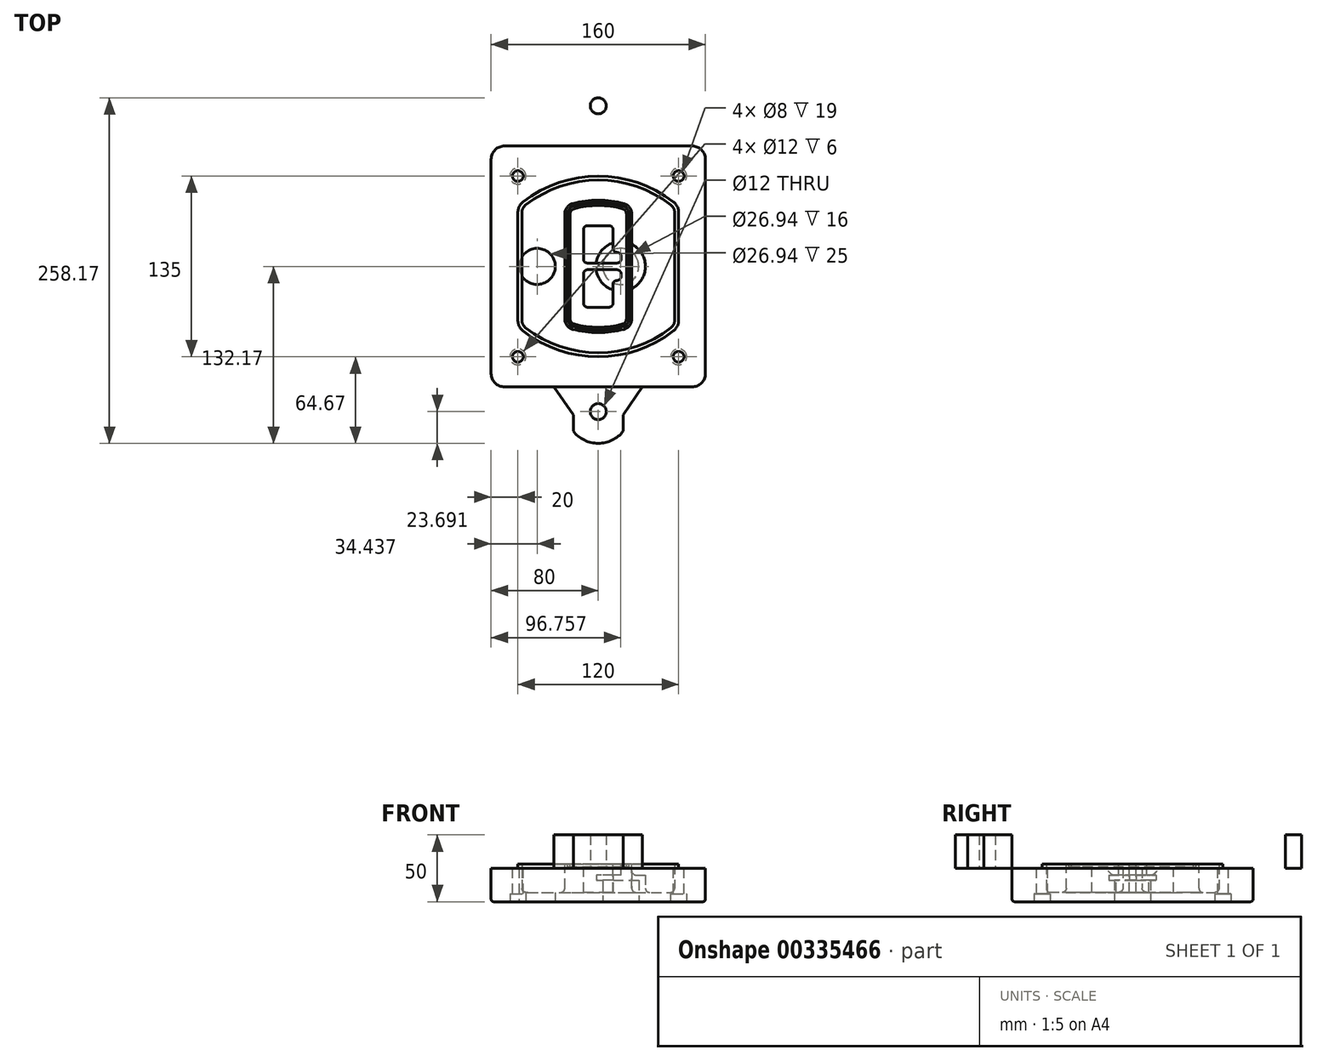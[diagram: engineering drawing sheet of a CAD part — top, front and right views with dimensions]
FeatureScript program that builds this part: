
annotation { "Feature Type Name" : "Feature", "Feature Type Description" : "" }
export const myFeature = defineFeature(function(context is Context, id is Id, definition is map)
    precondition{}
    {
        {
            var Q0;
            Q0=qCreatedBy(makeId("Top.planeOp"),FACE);
            var sketch = newSketch(context, id + "F0", { "sketchPlane" : qUnion([Q0])});
            skPoint(sketch, "E0.rect.middle", {"position": v(0, 0) * mm});
            skLineSegment(sketch, "E1.bottom", {"start": v(-70, -90) * mm, "end": v(70, -90) * mm});
            skLineSegment(sketch, "E1.top", {"start": v(-70, 90) * mm, "end": v(70, 90) * mm});
            skLineSegment(sketch, "E1.left", {"start": v(-80, -80) * mm, "end": v(-80, 80) * mm});
            skLineSegment(sketch, "E1.right", {"start": v(80, -80) * mm, "end": v(80, 80) * mm});
            skLineSegment(sketch, "E2", {"start": v(-80, 90) * mm, "end": v(80, -90) * mm, "construction": true});
            skLineSegment(sketch, "E3", {"start": v(80, 90) * mm, "end": v(-80, -90) * mm, "construction": true});
            skCircle(sketch, "E4", {"center": v(-60, 67.5) * mm, "radius": 4 * mm});
            skCircle(sketch, "E5", {"center": v(60, 67.5) * mm, "radius": 4 * mm});
            skCircle(sketch, "E6", {"center": v(60, -67.5) * mm, "radius": 4 * mm});
            skCircle(sketch, "E7", {"center": v(-60, -67.5) * mm, "radius": 4 * mm});
            skLineSegment(sketch, "E8", {"start": v(-60, 67.5) * mm, "end": v(60, 67.5) * mm, "construction": true});
            skLineSegment(sketch, "E9", {"start": v(60, 67.5) * mm, "end": v(60, -67.5) * mm, "construction": true});
            skLineSegment(sketch, "E10", {"start": v(60, -67.5) * mm, "end": v(-60, -67.5) * mm, "construction": true});
            skLineSegment(sketch, "E11", {"start": v(-60, -67.5) * mm, "end": v(-60, 67.5) * mm, "construction": true});
            skLineSegment(sketch, "E12", {"start": v(-60, 40.3) * mm, "end": v(-60, -40.3) * mm});
            skLineSegment(sketch, "E13", {"start": v(60, 40.3) * mm, "end": v(60, -40.3) * mm});
            skArc(sketch, "E14", {"start": v(56.15, 48.18) * mm, "mid": v(0, 67.5) * mm, "end": v(-56.15, 48.18) * mm});
            skArc(sketch, "E15", {"start": v(-56.15, -48.18) * mm, "mid": v(0, -67.5) * mm, "end": v(56.15, -48.18) * mm});
            skLineSegment(sketch, "E16", {"start": v(-60, 0) * mm, "end": v(60, 0) * mm, "construction": true});
            skPoint(sketch, "E17.visualSharp", {"position": v(-60, -45) * mm});
            skArc(sketch, "E17.filletArc", {"start": v(-60, -40.3) * mm, "mid": v(-58.99, -44.68) * mm, "end": v(-56.15, -48.18) * mm});
            skPoint(sketch, "E18.visualSharp", {"position": v(-60, 45) * mm});
            skArc(sketch, "E18.filletArc", {"start": v(-56.15, 48.18) * mm, "mid": v(-58.99, 44.68) * mm, "end": v(-60, 40.3) * mm});
            skPoint(sketch, "E19.visualSharp", {"position": v(60, 45) * mm});
            skArc(sketch, "E19.filletArc", {"start": v(60, 40.3) * mm, "mid": v(58.99, 44.68) * mm, "end": v(56.15, 48.18) * mm});
            skPoint(sketch, "E20.visualSharp", {"position": v(60, -45) * mm});
            skArc(sketch, "E20.filletArc", {"start": v(56.15, -48.18) * mm, "mid": v(58.99, -44.68) * mm, "end": v(60, -40.3) * mm});
            skPoint(sketch, "E21.visualSharp", {"position": v(-80, 90) * mm});
            skArc(sketch, "E21.filletArc", {"start": v(-70, 90) * mm, "mid": v(-77.07, 87.07) * mm, "end": v(-80, 80) * mm});
            skPoint(sketch, "E22.visualSharp", {"position": v(80, 90) * mm});
            skArc(sketch, "E22.filletArc", {"start": v(80, 80) * mm, "mid": v(77.07, 87.07) * mm, "end": v(70, 90) * mm});
            skPoint(sketch, "E23.visualSharp", {"position": v(80, -90) * mm});
            skArc(sketch, "E23.filletArc", {"start": v(70, -90) * mm, "mid": v(77.07, -87.07) * mm, "end": v(80, -80) * mm});
            skPoint(sketch, "E24.visualSharp", {"position": v(-80, -90) * mm});
            skArc(sketch, "E24.filletArc", {"start": v(-80, -80) * mm, "mid": v(-77.07, -87.07) * mm, "end": v(-70, -90) * mm});
            skArc(sketch, "E25.0", {"start": v(57, 40.3) * mm, "mid": v(56.3, 43.36) * mm, "end": v(54.3, 45.81) * mm});
            skLineSegment(sketch, "E25.1", {"start": v(57, 40.3) * mm, "end": v(57, -40.3) * mm});
            skArc(sketch, "E25.2", {"start": v(54.3, -45.81) * mm, "mid": v(56.3, -43.36) * mm, "end": v(57, -40.3) * mm});
            skArc(sketch, "E25.3", {"start": v(-54.3, -45.81) * mm, "mid": v(0, -64.5) * mm, "end": v(54.3, -45.81) * mm});
            skArc(sketch, "E25.4", {"start": v(-57, -40.3) * mm, "mid": v(-56.3, -43.36) * mm, "end": v(-54.3, -45.81) * mm});
            skArc(sketch, "E25.5", {"start": v(54.3, 45.81) * mm, "mid": v(0, 64.5) * mm, "end": v(-54.3, 45.81) * mm});
            skLineSegment(sketch, "E25.6", {"start": v(-57, 40.3) * mm, "end": v(-57, -40.3) * mm});
            skArc(sketch, "E25.7", {"start": v(-54.3, 45.81) * mm, "mid": v(-56.3, 43.36) * mm, "end": v(-57, 40.3) * mm});
            skArc(sketch, "E26.0", {"start": v(-58.62, 51.33) * mm, "mid": v(-62.58, 46.43) * mm, "end": v(-64, 40.3) * mm});
            skArc(sketch, "E26.1", {"start": v(58.62, 51.33) * mm, "mid": v(0, 71.5) * mm, "end": v(-58.62, 51.33) * mm});
            skArc(sketch, "E26.2", {"start": v(64, 40.3) * mm, "mid": v(62.58, 46.43) * mm, "end": v(58.62, 51.33) * mm});
            skLineSegment(sketch, "E26.3", {"start": v(64, 40.3) * mm, "end": v(64, -40.3) * mm});
            skArc(sketch, "E26.4", {"start": v(58.62, -51.33) * mm, "mid": v(62.58, -46.43) * mm, "end": v(64, -40.3) * mm});
            skLineSegment(sketch, "E26.5", {"start": v(-64, 40.3) * mm, "end": v(-64, -40.3) * mm});
            skArc(sketch, "E26.6", {"start": v(-58.62, -51.33) * mm, "mid": v(0, -71.5) * mm, "end": v(58.62, -51.33) * mm});
            skArc(sketch, "E26.7", {"start": v(-64, -40.3) * mm, "mid": v(-62.58, -46.43) * mm, "end": v(-58.62, -51.33) * mm});
            skSolve(sketch);
        }
        {
            var Q0;
            Q0=makeQuery(id+"F0.imprint","IMPRINT",FACE,{"disambiguationData":[TD([[makeQuery(id+"F0.imprint","IMPRINT",EDGE,{"derivedFrom":sQuery(id+"F0.wireOp",EDGE,"E1.bottom")}),1.0]])]});
            var Q1;
            Q1=makeQuery(id+"F0.imprint","IMPRINT",FACE,{"disambiguationData":[TD([[makeQuery(id+"F0.imprint","IMPRINT",EDGE,{"derivedFrom":sQuery(id+"F0.wireOp",EDGE,"E12")}),1.0]])]});
            var Q2;
            Q2=makeQuery(id+"F0.imprint","IMPRINT",FACE,{"disambiguationData":[TD([[makeQuery(id+"F0.imprint","IMPRINT",EDGE,{"derivedFrom":sQuery(id+"F0.wireOp",EDGE,"E25.0")}),1.0]])]});
            var Q3;
            Q3=makeQuery(id+"F0.imprint","IMPRINT",FACE,{"disambiguationData":[TD([[makeQuery(id+"F0.imprint","IMPRINT",EDGE,{"derivedFrom":sQuery(id+"F0.wireOp",EDGE,"E12")}),-1.0]])]});
            extrude(context, id + "F1", {"entities" : qUnion([Q0, Q1, Q2, Q3]), "oppositeDirection" : true, "depth" : 25 * mm});
        }
        {
            var Q0;
            Q0=makeQuery(id+"F0.imprint","IMPRINT",FACE,{"disambiguationData":[TD([[makeQuery(id+"F0.imprint","IMPRINT",EDGE,{"derivedFrom":sQuery(id+"F0.wireOp",EDGE,"E12")}),1.0]])]});
            extrude(context, id + "F2", {"entities" : qUnion([Q0]), "operationType" : NewBodyOperationType.ADD, "depth" : 3 * mm});
        }
        {
            var Q0;
            Q0=makeQuery(id+"F0.imprint","IMPRINT",FACE,{"disambiguationData":[TD([[makeQuery(id+"F0.imprint","IMPRINT",EDGE,{"derivedFrom":sQuery(id+"F0.wireOp",EDGE,"E25.0")}),1.0]])]});
            extrude(context, id + "F3", {"entities" : qUnion([Q0]), "operationType" : NewBodyOperationType.REMOVE, "oppositeDirection" : true, "depth" : 18 * mm});
        }
        {
            var Q0;
            Q0=makeQuery(id+"F2.opExtrude","CAP_FACE",FACE,{"disambiguationData":[OSD([sQuery(id+"F0.wireOp",EDGE,"E12"),sQuery(id+"F0.wireOp",EDGE,"E13"),sQuery(id+"F0.wireOp",EDGE,"E14"),sQuery(id+"F0.wireOp",EDGE,"E15"),sQuery(id+"F0.wireOp",EDGE,"E17.filletArc"),sQuery(id+"F0.wireOp",EDGE,"E18.filletArc"),sQuery(id+"F0.wireOp",EDGE,"E19.filletArc"),sQuery(id+"F0.wireOp",EDGE,"E20.filletArc"),sQuery(id+"F0.wireOp",EDGE,"E25.0"),sQuery(id+"F0.wireOp",EDGE,"E25.1"),sQuery(id+"F0.wireOp",EDGE,"E25.2"),sQuery(id+"F0.wireOp",EDGE,"E25.3"),sQuery(id+"F0.wireOp",EDGE,"E25.4"),sQuery(id+"F0.wireOp",EDGE,"E25.5"),sQuery(id+"F0.wireOp",EDGE,"E25.6"),sQuery(id+"F0.wireOp",EDGE,"E25.7")])],"isStart":false});
            var sketch = newSketch(context, id + "F4", { "sketchPlane" : qUnion([Q0])});
            skArc(sketch, "E27.0", {"start": v(-19.08, -46.97) * mm, "mid": v(0, -49.5) * mm, "end": v(19.08, -46.97) * mm});
            skArc(sketch, "E28.0", {"start": v(19.08, 46.97) * mm, "mid": v(0, 49.5) * mm, "end": v(-19.08, 46.97) * mm});
            skLineSegment(sketch, "E29", {"start": v(-25, 39.25) * mm, "end": v(-25, -39.25) * mm});
            skLineSegment(sketch, "E30", {"start": v(25, 39.25) * mm, "end": v(25, -39.25) * mm});
            skLineSegment(sketch, "E31", {"start": v(-25, 45.1) * mm, "end": v(25, 45.1) * mm, "construction": true});
            skLineSegment(sketch, "E32", {"start": v(-25, -45.1) * mm, "end": v(25, -45.1) * mm, "construction": true});
            skPoint(sketch, "E33.visualSharp", {"position": v(-25, 45.1) * mm});
            skArc(sketch, "E33.filletArc", {"start": v(-19.08, 46.97) * mm, "mid": v(-23.35, 44.11) * mm, "end": v(-25, 39.25) * mm});
            skPoint(sketch, "E34.visualSharp", {"position": v(25, 45.1) * mm});
            skArc(sketch, "E34.filletArc", {"start": v(25, 39.25) * mm, "mid": v(23.35, 44.11) * mm, "end": v(19.08, 46.97) * mm});
            skPoint(sketch, "E35.visualSharp", {"position": v(25, -45.1) * mm});
            skArc(sketch, "E35.filletArc", {"start": v(19.08, -46.97) * mm, "mid": v(23.35, -44.11) * mm, "end": v(25, -39.25) * mm});
            skPoint(sketch, "E36.visualSharp", {"position": v(-25, -45.1) * mm});
            skArc(sketch, "E36.filletArc", {"start": v(-25, -39.25) * mm, "mid": v(-23.35, -44.11) * mm, "end": v(-19.08, -46.97) * mm});
            skArc(sketch, "E37.0", {"start": v(54.3, 45.81) * mm, "mid": v(0, 64.5) * mm, "end": v(-54.3, 45.81) * mm});
            skArc(sketch, "E37.1", {"start": v(-54.3, 45.81) * mm, "mid": v(-56.3, 43.36) * mm, "end": v(-57, 40.3) * mm});
            skLineSegment(sketch, "E37.2", {"start": v(-57, 40.3) * mm, "end": v(-57, -40.3) * mm});
            skArc(sketch, "E37.3", {"start": v(-57, -40.3) * mm, "mid": v(-56.3, -43.36) * mm, "end": v(-54.3, -45.81) * mm});
            skArc(sketch, "E37.4", {"start": v(-54.3, -45.81) * mm, "mid": v(0, -64.5) * mm, "end": v(54.3, -45.81) * mm});
            skArc(sketch, "E37.5", {"start": v(54.3, -45.81) * mm, "mid": v(56.3, -43.36) * mm, "end": v(57, -40.3) * mm});
            skLineSegment(sketch, "E37.6", {"start": v(57, 40.3) * mm, "end": v(57, -40.3) * mm});
            skArc(sketch, "E37.7", {"start": v(57, 40.3) * mm, "mid": v(56.3, 43.36) * mm, "end": v(54.3, 45.81) * mm});
            skLineSegment(sketch, "E38.0", {"start": v(23, 39.25) * mm, "end": v(23, -39.25) * mm});
            skArc(sketch, "E38.1", {"start": v(18.56, -45.04) * mm, "mid": v(21.76, -42.9) * mm, "end": v(23, -39.25) * mm});
            skArc(sketch, "E38.2", {"start": v(-18.56, -45.04) * mm, "mid": v(0, -47.5) * mm, "end": v(18.56, -45.04) * mm});
            skArc(sketch, "E38.3", {"start": v(-23, -39.25) * mm, "mid": v(-21.76, -42.9) * mm, "end": v(-18.56, -45.04) * mm});
            skLineSegment(sketch, "E38.4", {"start": v(-23, 39.25) * mm, "end": v(-23, -39.25) * mm});
            skArc(sketch, "E38.5", {"start": v(23, 39.25) * mm, "mid": v(21.76, 42.9) * mm, "end": v(18.56, 45.04) * mm});
            skArc(sketch, "E38.6", {"start": v(-18.56, 45.04) * mm, "mid": v(-21.76, 42.9) * mm, "end": v(-23, 39.25) * mm});
            skArc(sketch, "E38.7", {"start": v(18.56, 45.04) * mm, "mid": v(0, 47.5) * mm, "end": v(-18.56, 45.04) * mm});
            skArc(sketch, "E39.0", {"start": v(21, 39.25) * mm, "mid": v(20.18, 41.68) * mm, "end": v(18.04, 43.1) * mm});
            skLineSegment(sketch, "E39.1", {"start": v(21, 39.25) * mm, "end": v(21, -39.25) * mm});
            skArc(sketch, "E39.2", {"start": v(18.04, -43.1) * mm, "mid": v(20.18, -41.68) * mm, "end": v(21, -39.25) * mm});
            skArc(sketch, "E39.3", {"start": v(-18.04, -43.1) * mm, "mid": v(0, -45.5) * mm, "end": v(18.04, -43.1) * mm});
            skArc(sketch, "E39.4", {"start": v(-21, -39.25) * mm, "mid": v(-20.18, -41.68) * mm, "end": v(-18.04, -43.1) * mm});
            skArc(sketch, "E39.5", {"start": v(18.04, 43.1) * mm, "mid": v(0, 45.5) * mm, "end": v(-18.04, 43.1) * mm});
            skLineSegment(sketch, "E39.6", {"start": v(-21, 39.25) * mm, "end": v(-21, -39.25) * mm});
            skArc(sketch, "E39.7", {"start": v(-18.04, 43.1) * mm, "mid": v(-20.18, 41.68) * mm, "end": v(-21, 39.25) * mm});
            skLineSegment(sketch, "E40", {"start": v(-25, 0) * mm, "end": v(25, 0) * mm, "construction": true});
            skLineSegment(sketch, "E41", {"start": v(-11, 5.5) * mm, "end": v(-11, 27.5) * mm});
            skLineSegment(sketch, "E42", {"start": v(-8, 30.5) * mm, "end": v(8, 30.5) * mm});
            skLineSegment(sketch, "E43", {"start": v(11, 27.5) * mm, "end": v(11, 13.5) * mm});
            skLineSegment(sketch, "E44", {"start": v(14, 10.5) * mm, "end": v(14, 10.5) * mm});
            skLineSegment(sketch, "E45", {"start": v(17, 7.5) * mm, "end": v(17, 5.5) * mm});
            skLineSegment(sketch, "E46", {"start": v(14, 2.5) * mm, "end": v(-8, 2.5) * mm});
            skPoint(sketch, "E47.visualSharp", {"position": v(-11, 30.5) * mm});
            skArc(sketch, "E47.filletArc", {"start": v(-8, 30.5) * mm, "mid": v(-10.12, 29.62) * mm, "end": v(-11, 27.5) * mm});
            skPoint(sketch, "E48.visualSharp", {"position": v(11, 30.5) * mm});
            skArc(sketch, "E48.filletArc", {"start": v(11, 27.5) * mm, "mid": v(10.12, 29.62) * mm, "end": v(8, 30.5) * mm});
            skPoint(sketch, "E49.visualSharp", {"position": v(11, 10.5) * mm});
            skArc(sketch, "E49.filletArc", {"start": v(11, 13.5) * mm, "mid": v(11.88, 11.38) * mm, "end": v(14, 10.5) * mm});
            skPoint(sketch, "E50.visualSharp", {"position": v(17, 10.5) * mm});
            skArc(sketch, "E50.filletArc", {"start": v(17, 7.5) * mm, "mid": v(16.12, 9.62) * mm, "end": v(14, 10.5) * mm});
            skPoint(sketch, "E51.visualSharp", {"position": v(17, 2.5) * mm});
            skArc(sketch, "E51.filletArc", {"start": v(14, 2.5) * mm, "mid": v(16.12, 3.38) * mm, "end": v(17, 5.5) * mm});
            skPoint(sketch, "E52.visualSharp", {"position": v(-11, 2.5) * mm});
            skArc(sketch, "E52.filletArc", {"start": v(-11, 5.5) * mm, "mid": v(-10.12, 3.38) * mm, "end": v(-8, 2.5) * mm});
            skLineSegment(sketch, "E53.0.MirrorCS", {"start": v(14, -2.5) * mm, "end": v(-8, -2.5) * mm});
            skArc(sketch, "E54.0.MirrorCS", {"start": v(-11, -5.5) * mm, "mid": v(-10.12, -3.38) * mm, "end": v(-8, -2.5) * mm});
            skLineSegment(sketch, "E55.0.MirrorCS", {"start": v(-11, -5.5) * mm, "end": v(-11, -27.5) * mm});
            skArc(sketch, "E56.0.MirrorCS", {"start": v(-8, -30.5) * mm, "mid": v(-10.12, -29.62) * mm, "end": v(-11, -27.5) * mm});
            skLineSegment(sketch, "E57.0.MirrorCS", {"start": v(-8, -30.5) * mm, "end": v(8, -30.5) * mm});
            skArc(sketch, "E58.0.MirrorCS", {"start": v(11, -27.5) * mm, "mid": v(10.12, -29.62) * mm, "end": v(8, -30.5) * mm});
            skLineSegment(sketch, "E59.0.MirrorCS", {"start": v(11, -27.5) * mm, "end": v(11, -13.5) * mm});
            skArc(sketch, "E60.0.MirrorCS", {"start": v(11, -13.5) * mm, "mid": v(11.88, -11.38) * mm, "end": v(14, -10.5) * mm});
            skArc(sketch, "E61.0.MirrorCS", {"start": v(17, -7.5) * mm, "mid": v(16.12, -9.62) * mm, "end": v(14, -10.5) * mm});
            skLineSegment(sketch, "E62.0.MirrorCS", {"start": v(17, -7.5) * mm, "end": v(17, -5.5) * mm});
            skArc(sketch, "E63.0.MirrorCS", {"start": v(14, -2.5) * mm, "mid": v(16.12, -3.38) * mm, "end": v(17, -5.5) * mm});
            skSolve(sketch);
        }
        {
            var Q0;
            Q0=makeQuery(id+"F4.imprint","IMPRINT",FACE,{"disambiguationData":[TD([[makeQuery(id+"F4.imprint","IMPRINT",EDGE,{"derivedFrom":sQuery(id+"F4.wireOp",EDGE,"E27.0")}),1.0]])]});
            var Q1;
            Q1=makeQuery(id+"F4.imprint","IMPRINT",FACE,{"disambiguationData":[TD([[makeQuery(id+"F4.imprint","IMPRINT",EDGE,{"derivedFrom":sQuery(id+"F4.wireOp",EDGE,"E38.0")}),-1.0]])]});
            var Q2;
            Q2=makeQuery(id+"F4.imprint","IMPRINT",FACE,{"disambiguationData":[TD([[makeQuery(id+"F4.imprint","IMPRINT",EDGE,{"derivedFrom":sQuery(id+"F4.wireOp",EDGE,"E39.0")}),1.0]])]});
            extrude(context, id + "F5", {"entities" : qUnion([Q0, Q1, Q2]), "operationType" : NewBodyOperationType.ADD, "endBound" : BoundingType.UP_TO_NEXT, "oppositeDirection" : true, "depth" : 25 * mm});
        }
        {
            var Q0;
            Q0=makeQuery(id+"F4.imprint","IMPRINT",FACE,{"disambiguationData":[TD([[makeQuery(id+"F4.imprint","IMPRINT",EDGE,{"derivedFrom":sQuery(id+"F4.wireOp",EDGE,"E38.0")}),-1.0]])]});
            extrude(context, id + "F6", {"entities" : qUnion([Q0]), "operationType" : NewBodyOperationType.REMOVE, "oppositeDirection" : true, "depth" : 2 * mm});
        }
        {
            var Q0;
            Q0=makeQuery(id+"F1.opExtrude","CAP_FACE",FACE,{"disambiguationData":[OSD([sQuery(id+"F0.wireOp",EDGE,"E1.bottom"),sQuery(id+"F0.wireOp",EDGE,"E1.top"),sQuery(id+"F0.wireOp",EDGE,"E1.left"),sQuery(id+"F0.wireOp",EDGE,"E1.right"),sQuery(id+"F0.wireOp",EDGE,"E4"),sQuery(id+"F0.wireOp",EDGE,"E5"),sQuery(id+"F0.wireOp",EDGE,"E6"),sQuery(id+"F0.wireOp",EDGE,"E7"),sQuery(id+"F0.wireOp",EDGE,"E21.filletArc"),sQuery(id+"F0.wireOp",EDGE,"E22.filletArc"),sQuery(id+"F0.wireOp",EDGE,"E23.filletArc"),sQuery(id+"F0.wireOp",EDGE,"E24.filletArc")])],"isStart":false});
            var sketch = newSketch(context, id + "F7", { "sketchPlane" : qUnion([Q0])});
            skCircle(sketch, "E64", {"center": v(16.76, 0) * mm, "radius": 13.47 * mm});
            skCircle(sketch, "E65", {"center": v(-45.56, 0) * mm, "radius": 13.47 * mm});
            skLineSegment(sketch, "E66", {"start": v(80, 0) * mm, "end": v(-80, 0) * mm});
            skCircle(sketch, "E67", {"center": v(16.76, 0) * mm, "radius": 18.47 * mm});
            skCircle(sketch, "E68", {"center": v(60, -67.5) * mm, "radius": 6 * mm});
            skCircle(sketch, "E69", {"center": v(-60, -67.5) * mm, "radius": 6 * mm});
            skCircle(sketch, "E70", {"center": v(-60, 67.5) * mm, "radius": 6 * mm});
            skCircle(sketch, "E71", {"center": v(60, 67.5) * mm, "radius": 6 * mm});
            skSolve(sketch);
        }
        {
            var Q0;
            {var subQ1=sQuery(id+"F7.wireOp",EDGE,"E66");var subQ4=sQuery(id+"F7.wireOp",EDGE,"E64");var subQ6=makeQuery(id+"F7.imprint","INTERSECT",VERTEX,{"disambiguationData":[OD(0.0)],"derivedFrom":[subQ4,subQ1]});Q0=makeQuery(id+"F7.imprint","IMPRINT",FACE,{"disambiguationData":[TD([[makeQuery(id+"F7.imprint","IMPRINT",EDGE,{"disambiguationData":[TD([[subQ6,-1.0]])],"derivedFrom":subQ4}),-1.0]])]});}
            var Q1;
            {var subQ0=sQuery(id+"F7.wireOp",EDGE,"E66");var subQ1=sQuery(id+"F7.wireOp",EDGE,"E64");var subQ3=makeQuery(id+"F7.imprint","INTERSECT",VERTEX,{"disambiguationData":[OD(0.0)],"derivedFrom":[subQ1,subQ0]});Q1=makeQuery(id+"F7.imprint","IMPRINT",FACE,{"disambiguationData":[TD([[makeQuery(id+"F7.imprint","IMPRINT",EDGE,{"disambiguationData":[TD([[subQ3,-1.0]])],"derivedFrom":subQ1}),1.0]])]});}
            var Q2;
            {var subQ0=sQuery(id+"F7.wireOp",EDGE,"E66");var subQ1=sQuery(id+"F7.wireOp",EDGE,"E64");var subQ3=makeQuery(id+"F7.imprint","INTERSECT",VERTEX,{"disambiguationData":[OD(0.0)],"derivedFrom":[subQ1,subQ0]});Q2=makeQuery(id+"F7.imprint","IMPRINT",FACE,{"disambiguationData":[TD([[makeQuery(id+"F7.imprint","IMPRINT",EDGE,{"disambiguationData":[TD([[subQ3,1.0]])],"derivedFrom":subQ1}),1.0]])]});}
            var Q3;
            {var subQ1=sQuery(id+"F7.wireOp",EDGE,"E66");var subQ4=sQuery(id+"F7.wireOp",EDGE,"E64");var subQ6=makeQuery(id+"F7.imprint","INTERSECT",VERTEX,{"disambiguationData":[OD(0.0)],"derivedFrom":[subQ4,subQ1]});Q3=makeQuery(id+"F7.imprint","IMPRINT",FACE,{"disambiguationData":[TD([[makeQuery(id+"F7.imprint","IMPRINT",EDGE,{"disambiguationData":[TD([[subQ6,1.0]])],"derivedFrom":subQ4}),-1.0]])]});}
            extrude(context, id + "F8", {"entities" : qUnion([Q0, Q1, Q2, Q3]), "operationType" : NewBodyOperationType.ADD, "oppositeDirection" : true, "depth" : 20 * mm});
        }
        {
            var Q0;
            {var subQ0=sQuery(id+"F7.wireOp",EDGE,"E66");var subQ1=sQuery(id+"F7.wireOp",EDGE,"E64");var subQ3=makeQuery(id+"F7.imprint","INTERSECT",VERTEX,{"disambiguationData":[OD(0.0)],"derivedFrom":[subQ1,subQ0]});Q0=makeQuery(id+"F7.imprint","IMPRINT",FACE,{"disambiguationData":[TD([[makeQuery(id+"F7.imprint","IMPRINT",EDGE,{"disambiguationData":[TD([[subQ3,-1.0]])],"derivedFrom":subQ1}),1.0]])]});}
            var Q1;
            {var subQ0=sQuery(id+"F7.wireOp",EDGE,"E66");var subQ1=sQuery(id+"F7.wireOp",EDGE,"E64");var subQ3=makeQuery(id+"F7.imprint","INTERSECT",VERTEX,{"disambiguationData":[OD(0.0)],"derivedFrom":[subQ1,subQ0]});Q1=makeQuery(id+"F7.imprint","IMPRINT",FACE,{"disambiguationData":[TD([[makeQuery(id+"F7.imprint","IMPRINT",EDGE,{"disambiguationData":[TD([[subQ3,1.0]])],"derivedFrom":subQ1}),1.0]])]});}
            extrude(context, id + "F9", {"entities" : qUnion([Q0, Q1]), "operationType" : NewBodyOperationType.REMOVE, "oppositeDirection" : true, "depth" : 16 * mm});
        }
        {
            var Q0;
            {var subQ0=sQuery(id+"F7.wireOp",EDGE,"E66");var subQ1=sQuery(id+"F7.wireOp",EDGE,"E65");var subQ3=makeQuery(id+"F7.imprint","INTERSECT",VERTEX,{"disambiguationData":[OD(0.0)],"derivedFrom":[subQ1,subQ0]});Q0=makeQuery(id+"F7.imprint","IMPRINT",FACE,{"disambiguationData":[TD([[makeQuery(id+"F7.imprint","IMPRINT",EDGE,{"disambiguationData":[TD([[subQ3,-1.0]])],"derivedFrom":subQ1}),1.0]])]});}
            var Q1;
            {var subQ0=sQuery(id+"F7.wireOp",EDGE,"E66");var subQ1=sQuery(id+"F7.wireOp",EDGE,"E65");var subQ3=makeQuery(id+"F7.imprint","INTERSECT",VERTEX,{"disambiguationData":[OD(0.0)],"derivedFrom":[subQ1,subQ0]});Q1=makeQuery(id+"F7.imprint","IMPRINT",FACE,{"disambiguationData":[TD([[makeQuery(id+"F7.imprint","IMPRINT",EDGE,{"disambiguationData":[TD([[subQ3,1.0]])],"derivedFrom":subQ1}),1.0]])]});}
            extrude(context, id + "F10", {"entities" : qUnion([Q0, Q1]), "operationType" : NewBodyOperationType.REMOVE, "oppositeDirection" : true, "depth" : 25 * mm});
        }
        {
            var Q0;
            Q0=makeQuery(id+"F7.imprint","IMPRINT",FACE,{"disambiguationData":[TD([[makeQuery(id+"F7.imprint","IMPRINT",EDGE,{"derivedFrom":sQuery(id+"F7.wireOp",EDGE,"E68")}),1.0]])]});
            var Q1;
            Q1=makeQuery(id+"F7.imprint","IMPRINT",FACE,{"disambiguationData":[TD([[makeQuery(id+"F7.imprint","IMPRINT",EDGE,{"derivedFrom":makeQuery(id+"F1.opExtrude","CAP_EDGE",EDGE,{"disambiguationData":[OSD([sQuery(id+"F0.wireOp",EDGE,"E5")])],"isStart":false})}),-1.0]])]});
            var Q2;
            Q2=makeQuery(id+"F7.imprint","IMPRINT",FACE,{"disambiguationData":[TD([[makeQuery(id+"F7.imprint","IMPRINT",EDGE,{"derivedFrom":sQuery(id+"F7.wireOp",EDGE,"E69")}),1.0]])]});
            var Q3;
            Q3=makeQuery(id+"F7.imprint","IMPRINT",FACE,{"disambiguationData":[TD([[makeQuery(id+"F7.imprint","IMPRINT",EDGE,{"derivedFrom":makeQuery(id+"F1.opExtrude","CAP_EDGE",EDGE,{"disambiguationData":[OSD([sQuery(id+"F0.wireOp",EDGE,"E4")])],"isStart":false})}),-1.0]])]});
            var Q4;
            Q4=makeQuery(id+"F7.imprint","IMPRINT",FACE,{"disambiguationData":[TD([[makeQuery(id+"F7.imprint","IMPRINT",EDGE,{"derivedFrom":sQuery(id+"F7.wireOp",EDGE,"E70")}),1.0]])]});
            var Q5;
            Q5=makeQuery(id+"F7.imprint","IMPRINT",FACE,{"disambiguationData":[TD([[makeQuery(id+"F7.imprint","IMPRINT",EDGE,{"derivedFrom":makeQuery(id+"F1.opExtrude","CAP_EDGE",EDGE,{"disambiguationData":[OSD([sQuery(id+"F0.wireOp",EDGE,"E7")])],"isStart":false})}),-1.0]])]});
            var Q6;
            Q6=makeQuery(id+"F7.imprint","IMPRINT",FACE,{"disambiguationData":[TD([[makeQuery(id+"F7.imprint","IMPRINT",EDGE,{"derivedFrom":sQuery(id+"F7.wireOp",EDGE,"E71")}),1.0]])]});
            var Q7;
            Q7=makeQuery(id+"F7.imprint","IMPRINT",FACE,{"disambiguationData":[TD([[makeQuery(id+"F7.imprint","IMPRINT",EDGE,{"derivedFrom":makeQuery(id+"F1.opExtrude","CAP_EDGE",EDGE,{"disambiguationData":[OSD([sQuery(id+"F0.wireOp",EDGE,"E6")])],"isStart":false})}),-1.0]])]});
            extrude(context, id + "F11", {"entities" : qUnion([Q0, Q1, Q2, Q3, Q4, Q5, Q6, Q7]), "operationType" : NewBodyOperationType.REMOVE, "oppositeDirection" : true, "depth" : 6 * mm});
        }
        {
            var Q0;
            Q0=makeQuery(id+"F9.boolean.opBoolean","COPY",FACE,{"derivedFrom":makeQuery(id+"F9.opExtrude","CAP_FACE",FACE,{"disambiguationData":[OSD([sQuery(id+"F7.wireOp",EDGE,"E64")])],"isStart":false})});
            var sketch = newSketch(context, id + "F12", { "sketchPlane" : qUnion([Q0])});
            skArc(sketch, "E72.0", {"start": v(11, 17.55) * mm, "mid": v(2.57, 11.82) * mm, "end": v(-1.54, 2.5) * mm});
            skArc(sketch, "E72.1", {"start": v(-1.54, -2.5) * mm, "mid": v(2.57, -11.82) * mm, "end": v(11, -17.55) * mm});
            skLineSegment(sketch, "E73", {"start": v(-1.54, -2.5) * mm, "end": v(14, -2.5) * mm});
            skLineSegment(sketch, "E74.0", {"start": v(14, 2.5) * mm, "end": v(-1.54, 2.5) * mm});
            skArc(sketch, "E74.1", {"start": v(14, 2.5) * mm, "mid": v(16.12, 3.38) * mm, "end": v(17, 5.5) * mm});
            skLineSegment(sketch, "E74.2", {"start": v(17, 7.5) * mm, "end": v(17, 5.5) * mm});
            skArc(sketch, "E74.3", {"start": v(17, 7.5) * mm, "mid": v(16.12, 9.62) * mm, "end": v(14, 10.5) * mm});
            skArc(sketch, "E74.4", {"start": v(11, 13.5) * mm, "mid": v(11.88, 11.38) * mm, "end": v(14, 10.5) * mm});
            skLineSegment(sketch, "E74.5", {"start": v(11, 17.55) * mm, "end": v(11, 13.5) * mm});
            skLineSegment(sketch, "E74.7", {"start": v(14, -2.5) * mm, "end": v(-1.54, -2.5) * mm});
            skArc(sketch, "E74.8", {"start": v(14, -2.5) * mm, "mid": v(16.12, -3.38) * mm, "end": v(17, -5.5) * mm});
            skLineSegment(sketch, "E74.9", {"start": v(17, -7.5) * mm, "end": v(17, -5.5) * mm});
            skArc(sketch, "E74.10", {"start": v(17, -7.5) * mm, "mid": v(16.12, -9.62) * mm, "end": v(14, -10.5) * mm});
            skArc(sketch, "E74.11", {"start": v(11, -13.5) * mm, "mid": v(11.88, -11.38) * mm, "end": v(14, -10.5) * mm});
            skLineSegment(sketch, "E74.12", {"start": v(11, -17.55) * mm, "end": v(11, -13.5) * mm});
            skPoint(sketch, "E75.orphan", {"position": v(11, -27.5) * mm});
            skPoint(sketch, "E76.orphan", {"position": v(-8, -2.5) * mm});
            skPoint(sketch, "E77.orphan", {"position": v(-8, 2.5) * mm});
            skPoint(sketch, "E78.orphan", {"position": v(11, 27.5) * mm});
            skSolve(sketch);
        }
        {
            var Q0;
            {var subQ7=sQuery(id+"F12.wireOp",EDGE,"E72.0");var subQ14=sQuery(id+"F12.wireOp",EDGE,"E72.1");var subQ16=sQuery(id+"F12.wireOp",EDGE,"E74.1");var subQ18=sQuery(id+"F12.wireOp",EDGE,"E74.8");Q0=qUnion([makeQuery(id+"F12.imprint","IMPRINT",FACE,{"disambiguationData":[TD([[makeQuery(id+"F12.imprint","IMPRINT",EDGE,{"derivedFrom":subQ7}),1.0]])]}),makeQuery(id+"F12.imprint","IMPRINT",FACE,{"disambiguationData":[TD([[makeQuery(id+"F12.imprint","IMPRINT",EDGE,{"derivedFrom":subQ14}),1.0]])]}),makeQuery(id+"F12.imprint","IMPRINT",FACE,{"disambiguationData":[TD([[makeQuery(id+"F12.imprint","IMPRINT",EDGE,{"derivedFrom":subQ16}),1.0]])]}),makeQuery(id+"F12.imprint","IMPRINT",FACE,{"disambiguationData":[TD([[makeQuery(id+"F12.imprint","IMPRINT",EDGE,{"derivedFrom":subQ18}),-1.0]])]})]);}
            var Q1;
            Q1=makeQuery(id+"F5.boolean.opBoolean","SPLIT",FACE,{"disambiguationData":[TD([makeQuery(id+"F5.opExtrude","SWEPT_FACE",FACE,{"disambiguationData":[OSD([sQuery(id+"F4.wireOp",EDGE,"E41")])]})])],"derivedFrom":makeQuery(id+"F3.boolean.opBoolean","COPY",FACE,{"derivedFrom":makeQuery(id+"F3.opExtrude","CAP_FACE",FACE,{"disambiguationData":[OSD([sQuery(id+"F0.wireOp",EDGE,"E25.0"),sQuery(id+"F0.wireOp",EDGE,"E25.1"),sQuery(id+"F0.wireOp",EDGE,"E25.2"),sQuery(id+"F0.wireOp",EDGE,"E25.3"),sQuery(id+"F0.wireOp",EDGE,"E25.4"),sQuery(id+"F0.wireOp",EDGE,"E25.5"),sQuery(id+"F0.wireOp",EDGE,"E25.6"),sQuery(id+"F0.wireOp",EDGE,"E25.7")])],"isStart":false})})});
            extrude(context, id + "F13", {"entities" : qUnion([Q0]), "operationType" : NewBodyOperationType.REMOVE, "endBound" : BoundingType.UP_TO_SURFACE, "endBoundEntityFace" : qUnion([Q1]), "depth" : 25 * mm});
        }
        {
            var Q0;
            Q0=makeQuery(id+"F3.boolean.opBoolean","COPY",EDGE,{"derivedFrom":makeQuery(id+"F3.opExtrude","CAP_EDGE",EDGE,{"disambiguationData":[OSD([sQuery(id+"F0.wireOp",EDGE,"E25.6")])],"isStart":false})});
            var Q1;
            Q1=makeQuery(id+"F8.boolean.opBoolean","INTERSECT",EDGE,{"derivedFrom":[makeQuery(id+"F5.opExtrude","SWEPT_FACE",FACE,{"disambiguationData":[OSD([sQuery(id+"F4.wireOp",EDGE,"E30")])]}),makeQuery(id+"F8.opExtrude","CAP_FACE",FACE,{"disambiguationData":[OSD([sQuery(id+"F7.wireOp",EDGE,"E67")])],"isStart":false})]});
            var Q2;
            Q2=makeQuery(id+"F8.boolean.opBoolean","INTERSECT",EDGE,{"disambiguationData":[OD(1.0)],"derivedFrom":[makeQuery(id+"F5.opExtrude","SWEPT_FACE",FACE,{"disambiguationData":[OSD([sQuery(id+"F4.wireOp",EDGE,"E30")])]}),makeQuery(id+"F8.opExtrude","SWEPT_FACE",FACE,{"disambiguationData":[OSD([sQuery(id+"F7.wireOp",EDGE,"E67")])]})]});
            var Q3;
            {var subQ0=sQuery(id+"F4.wireOp",EDGE,"E30");Q3=makeQuery(id+"F8.boolean.opBoolean","SPLIT",EDGE,{"disambiguationData":[TD([makeQuery(id+"F5.opExtrude","SWEPT_FACE",FACE,{"disambiguationData":[OSD([sQuery(id+"F4.wireOp",EDGE,"E35.filletArc")])]})])],"derivedFrom":makeQuery(id+"F5.opExtrude","CAP_EDGE",EDGE,{"disambiguationData":[OSD([subQ0])],"isStart":false})});}
            var Q4;
            {var subQ0=sQuery(id+"F0.wireOp",EDGE,"E25.7");var subQ1=sQuery(id+"F0.wireOp",EDGE,"E25.1");var subQ2=sQuery(id+"F0.wireOp",EDGE,"E25.6");var subQ3=sQuery(id+"F0.wireOp",EDGE,"E25.5");var subQ4=sQuery(id+"F0.wireOp",EDGE,"E25.4");var subQ5=sQuery(id+"F0.wireOp",EDGE,"E25.0");var subQ6=sQuery(id+"F0.wireOp",EDGE,"E25.2");var subQ7=sQuery(id+"F0.wireOp",EDGE,"E25.3");Q4=makeQuery(id+"F8.boolean.opBoolean","INTERSECT",EDGE,{"derivedFrom":[makeQuery(id+"F5.boolean.opBoolean","SPLIT",FACE,{"disambiguationData":[TD([makeQuery(id+"F2.opExtrude","SWEPT_FACE",FACE,{"disambiguationData":[OSD([subQ5])]})])],"derivedFrom":makeQuery(id+"F3.boolean.opBoolean","COPY",FACE,{"derivedFrom":makeQuery(id+"F3.opExtrude","CAP_FACE",FACE,{"disambiguationData":[OSD([subQ5,subQ1,subQ6,subQ7,subQ4,subQ3,subQ2,subQ0])],"isStart":false})})}),makeQuery(id+"F8.opExtrude","SWEPT_FACE",FACE,{"disambiguationData":[OSD([sQuery(id+"F7.wireOp",EDGE,"E67")])]})]});}
            var Q5;
            Q5=makeQuery(id+"F8.boolean.opBoolean","INTERSECT",EDGE,{"disambiguationData":[OD(0.0)],"derivedFrom":[makeQuery(id+"F5.opExtrude","SWEPT_FACE",FACE,{"disambiguationData":[OSD([sQuery(id+"F4.wireOp",EDGE,"E30")])]}),makeQuery(id+"F8.opExtrude","SWEPT_FACE",FACE,{"disambiguationData":[OSD([sQuery(id+"F7.wireOp",EDGE,"E67")])]})]});
            fillet(context, id + "F14", {"entities" : qUnion([Q0, Q1, Q2, Q3, Q4, Q5]), "radius" : 3 * mm, "tangentPropagation" : true, "allowEdgeOverflow" : false});
        }
        {
            var Q0;
            Q0=makeQuery(id+"F1.opExtrude","CAP_EDGE",EDGE,{"disambiguationData":[OSD([sQuery(id+"F0.wireOp",EDGE,"E1.bottom")])],"isStart":false});
            fillet(context, id + "F15", {"entities" : qUnion([Q0]), "radius" : 2 * mm, "tangentPropagation" : true, "allowEdgeOverflow" : false});
        }
        {
            var Q0;
            {var subQ0=sQuery(id+"F0.wireOp",EDGE,"E21.filletArc");var subQ1=sQuery(id+"F0.wireOp",EDGE,"E7");var subQ2=sQuery(id+"F0.wireOp",EDGE,"E6");var subQ3=sQuery(id+"F0.wireOp",EDGE,"E5");var subQ4=sQuery(id+"F0.wireOp",EDGE,"E4");var subQ5=sQuery(id+"F0.wireOp",EDGE,"E22.filletArc");var subQ6=sQuery(id+"F0.wireOp",EDGE,"E1.bottom");var subQ7=sQuery(id+"F0.wireOp",EDGE,"E1.right");var subQ8=sQuery(id+"F0.wireOp",EDGE,"E1.top");var subQ9=sQuery(id+"F0.wireOp",EDGE,"E1.left");var subQ10=sQuery(id+"F0.wireOp",EDGE,"E23.filletArc");var subQ11=sQuery(id+"F0.wireOp",EDGE,"E24.filletArc");Q0=makeQuery(id+"F2.boolean.opBoolean","SPLIT",FACE,{"disambiguationData":[TD([makeQuery(id+"F1.opExtrude","SWEPT_FACE",FACE,{"disambiguationData":[OSD([subQ6])]})])],"derivedFrom":makeQuery(id+"F1.opExtrude","CAP_FACE",FACE,{"disambiguationData":[OSD([subQ6,subQ8,subQ9,subQ7,subQ4,subQ3,subQ2,subQ1,subQ0,subQ5,subQ10,subQ11])],"isStart":true})});}
            var sketch = newSketch(context, id + "F16", { "sketchPlane" : qUnion([Q0])});
            skLineSegment(sketch, "E79", {"start": v(0, 90) * mm, "end": v(0, 120) * mm, "construction": true});
            skCircle(sketch, "E80", {"center": v(0, 120) * mm, "radius": 6 * mm});
            skLineSegment(sketch, "E81", {"start": v(-33, 90) * mm, "end": v(-15, 108) * mm});
            skLineSegment(sketch, "E82", {"start": v(-15, 108) * mm, "end": v(-15, 120) * mm});
            skLineSegment(sketch, "E83", {"start": v(33, 90) * mm, "end": v(15, 108) * mm});
            skLineSegment(sketch, "E84", {"start": v(15, 108) * mm, "end": v(15, 120) * mm});
            skArc(sketch, "E85", {"start": v(15, 120) * mm, "mid": v(0, 135) * mm, "end": v(-15, 120) * mm});
            skArc(sketch, "E86.MirrorCS", {"start": v(-15, 120) * mm, "mid": v(0, 135) * mm, "end": v(15, 120) * mm});
            skLineSegment(sketch, "E87", {"start": v(33, -90) * mm, "end": v(18.69, -111.05) * mm});
            skLineSegment(sketch, "E88", {"start": v(-33, -90) * mm, "end": v(-18.69, -111.05) * mm});
            skLineSegment(sketch, "E89", {"start": v(-18.69, -111.05) * mm, "end": v(-18.69, -123.05) * mm});
            skLineSegment(sketch, "E90", {"start": v(18.69, -111.05) * mm, "end": v(18.69, -123.05) * mm});
            skArc(sketch, "E91", {"start": v(-18.69, -123.05) * mm, "mid": v(0, -132.17) * mm, "end": v(18.69, -123.05) * mm});
            skCircle(sketch, "E92", {"center": v(0, -108.48) * mm, "radius": 6 * mm});
            skLineSegment(sketch, "E93", {"start": v(0, -108.48) * mm, "end": v(0, -90) * mm, "construction": true});
            skSolve(sketch);
        }
        {
            var Q0;
            Q0=makeQuery(id+"F16.imprint","IMPRINT",FACE,{"disambiguationData":[TD([[makeQuery(id+"F16.imprint","IMPRINT",EDGE,{"derivedFrom":sQuery(id+"F16.wireOp",EDGE,"E80")}),1.0]])]});
            var Q1;
            {var subQ1=sQuery(id+"F16.wireOp",EDGE,"E87");Q1=makeQuery(id+"F16.imprint","IMPRINT",FACE,{"disambiguationData":[TD([[makeQuery(id+"F16.imprint","IMPRINT",EDGE,{"derivedFrom":subQ1}),-1.0]])]});}
            extrude(context, id + "F17", {"entities" : qUnion([Q0, Q1]), "depth" : 25 * mm});
        }
    });
